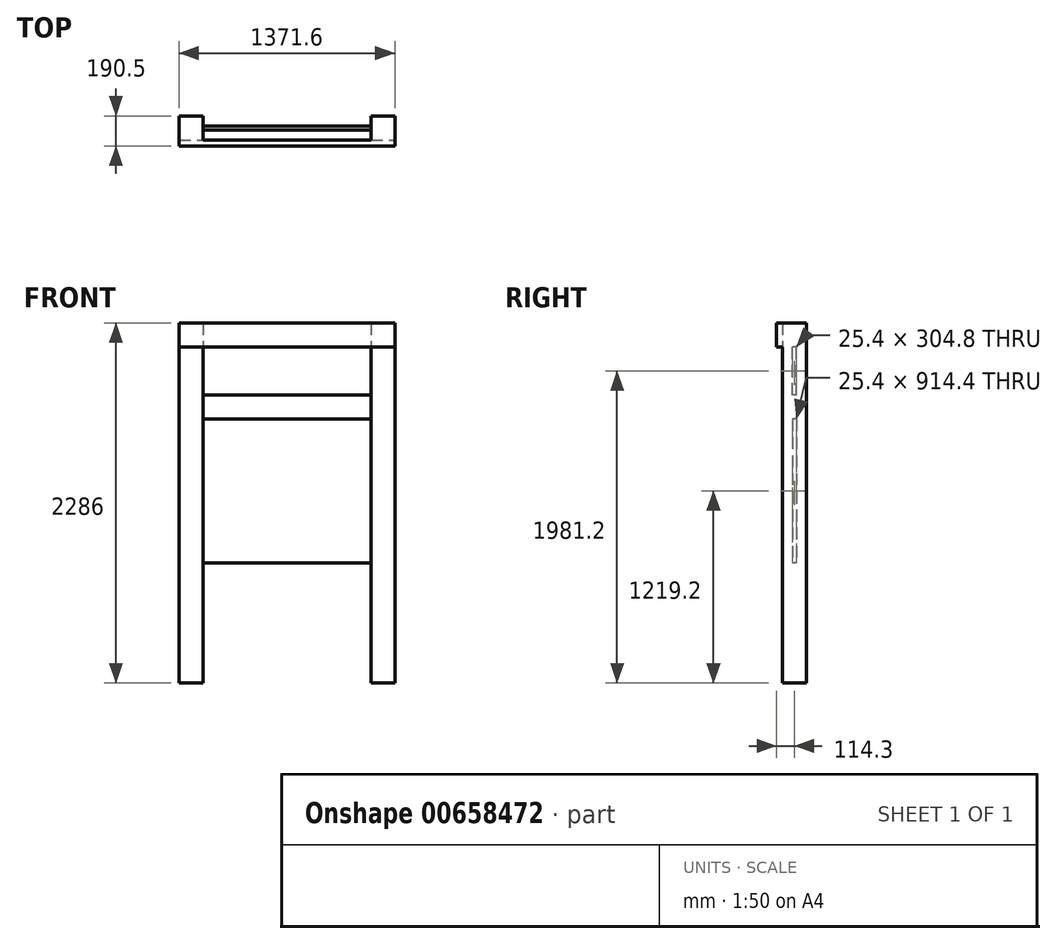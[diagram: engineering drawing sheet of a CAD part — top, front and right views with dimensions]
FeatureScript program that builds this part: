
annotation { "Feature Type Name" : "Feature", "Feature Type Description" : "" }
export const myFeature = defineFeature(function(context is Context, id is Id, definition is map)
    precondition{}
    {
        {
            var Q0;
            Q0=qCreatedBy(makeId("Top.planeOp"),FACE);
            var sketch = newSketch(context, id + "F0", { "sketchPlane" : qUnion([Q0])});
            skLineSegment(sketch, "E0.bottom", {"start": v(0, 0) * mm, "end": v(152.4, 0) * mm});
            skLineSegment(sketch, "E0.top", {"start": v(0, -152.4) * mm, "end": v(152.4, -152.4) * mm});
            skLineSegment(sketch, "E0.left", {"start": v(0, 0) * mm, "end": v(0, -152.4) * mm});
            skLineSegment(sketch, "E0.right", {"start": v(152.4, 0) * mm, "end": v(152.4, -152.4) * mm});
            skSolve(sketch);
        }
        {
            var Q0;
            Q0=makeQuery(id+"F0.imprint","IMPRINT",FACE,{"disambiguationData":[TD([[makeQuery(id+"F0.imprint","IMPRINT",EDGE,{"derivedFrom":sQuery(id+"F0.wireOp",EDGE,"E0.bottom")}),-1.0]])]});
            extrude(context, id + "F1", {"entities" : qUnion([Q0]), "depth" : 2286 * mm, "offsetDistance" : 25.4 * mm});
        }
        {
            var Q0;
            Q0=makeQuery(id+"F1.opExtrude","SWEPT_FACE",FACE,{"disambiguationData":[OSD([sQuery(id+"F0.wireOp",EDGE,"E0.right")])]});
            var sketch = newSketch(context, id + "F2", { "sketchPlane" : qUnion([Q0])});
            skLineSegment(sketch, "E1.bottom", {"start": v(-63.5, 1676.4) * mm, "end": v(-88.9, 1676.4) * mm});
            skLineSegment(sketch, "E1.top", {"start": v(-63.5, 762) * mm, "end": v(-88.9, 762) * mm});
            skLineSegment(sketch, "E1.left", {"start": v(-63.5, 1676.4) * mm, "end": v(-63.5, 762) * mm});
            skLineSegment(sketch, "E1.right", {"start": v(-88.9, 1676.4) * mm, "end": v(-88.9, 762) * mm});
            skLineSegment(sketch, "E2.bottom", {"start": v(-63.5, 1828.8) * mm, "end": v(-88.9, 1828.8) * mm});
            skLineSegment(sketch, "E2.top", {"start": v(-63.5, 2133.6) * mm, "end": v(-88.9, 2133.6) * mm});
            skLineSegment(sketch, "E2.left", {"start": v(-63.5, 1828.8) * mm, "end": v(-63.5, 2133.6) * mm});
            skLineSegment(sketch, "E2.right", {"start": v(-88.9, 1828.8) * mm, "end": v(-88.9, 2133.6) * mm});
            skSolve(sketch);
        }
        {
            var Q0;
            Q0=makeQuery(id+"F2.imprint","IMPRINT",FACE,{"disambiguationData":[TD([[makeQuery(id+"F2.imprint","IMPRINT",EDGE,{"derivedFrom":sQuery(id+"F2.wireOp",EDGE,"E1.bottom")}),1.0]])]});
            var Q1;
            Q1=makeQuery(id+"F2.imprint","IMPRINT",FACE,{"disambiguationData":[TD([[makeQuery(id+"F2.imprint","IMPRINT",EDGE,{"derivedFrom":sQuery(id+"F2.wireOp",EDGE,"E2.bottom")}),-1.0]])]});
            extrude(context, id + "F3", {"entities" : qUnion([Q0, Q1]), "operationType" : NewBodyOperationType.ADD, "depth" : 533.4 * mm, "offsetDistance" : 25.4 * mm});
        }
        {
            var Q0;
            Q0=makeQuery(id+"F1.opExtrude","SWEPT_BODY",BODY,{"disambiguationData":[OSD([sQuery(id+"F0.wireOp",EDGE,"E0.bottom"),sQuery(id+"F0.wireOp",EDGE,"E0.top"),sQuery(id+"F0.wireOp",EDGE,"E0.left"),sQuery(id+"F0.wireOp",EDGE,"E0.right")])]});
            var Q1;
            Q1=makeQuery(id+"F3.opExtrude","CAP_FACE",FACE,{"disambiguationData":[OSD([sQuery(id+"F2.wireOp",EDGE,"E1.bottom"),sQuery(id+"F2.wireOp",EDGE,"E1.top"),sQuery(id+"F2.wireOp",EDGE,"E1.left"),sQuery(id+"F2.wireOp",EDGE,"E1.right")])],"isStart":false});
            mirror(context, id + "F4", {"operationType" : NewBodyOperationType.ADD, "entities" : qUnion([Q0]), "mirrorPlane" : qUnion([Q1])});
        }
        {
            var Q0;
            Q0=makeQuery(id+"F1.opExtrude","SWEPT_FACE",FACE,{"disambiguationData":[OSD([sQuery(id+"F0.wireOp",EDGE,"E0.top")])]});
            var sketch = newSketch(context, id + "F5", { "sketchPlane" : qUnion([Q0])});
            skLineSegment(sketch, "E3.bottom", {"start": v(0, 2286) * mm, "end": v(1371.6, 2286) * mm});
            skLineSegment(sketch, "E3.top", {"start": v(0, 2133.6) * mm, "end": v(1371.6, 2133.6) * mm});
            skLineSegment(sketch, "E3.left", {"start": v(0, 2286) * mm, "end": v(0, 2133.6) * mm});
            skLineSegment(sketch, "E3.right", {"start": v(1371.6, 2286) * mm, "end": v(1371.6, 2133.6) * mm});
            skSolve(sketch);
        }
        {
            var Q0;
            {var subQ3=sQuery(id+"F5.wireOp",EDGE,"E3.right");Q0=makeQuery(id+"F5.imprint","IMPRINT",FACE,{"disambiguationData":[TD([[makeQuery(id+"F5.imprint","IMPRINT",EDGE,{"derivedFrom":subQ3}),-1.0]])]});}
            var Q1;
            {var subQ0=sQuery(id+"F5.wireOp",EDGE,"E3.left");Q1=makeQuery(id+"F5.imprint","IMPRINT",FACE,{"disambiguationData":[TD([[makeQuery(id+"F5.imprint","IMPRINT",EDGE,{"derivedFrom":subQ0}),1.0]])]});}
            extrude(context, id + "F6", {"entities" : qUnion([Q0, Q1]), "operationType" : NewBodyOperationType.ADD, "depth" : 38.1 * mm, "offsetDistance" : 25.4 * mm});
        }
    });
